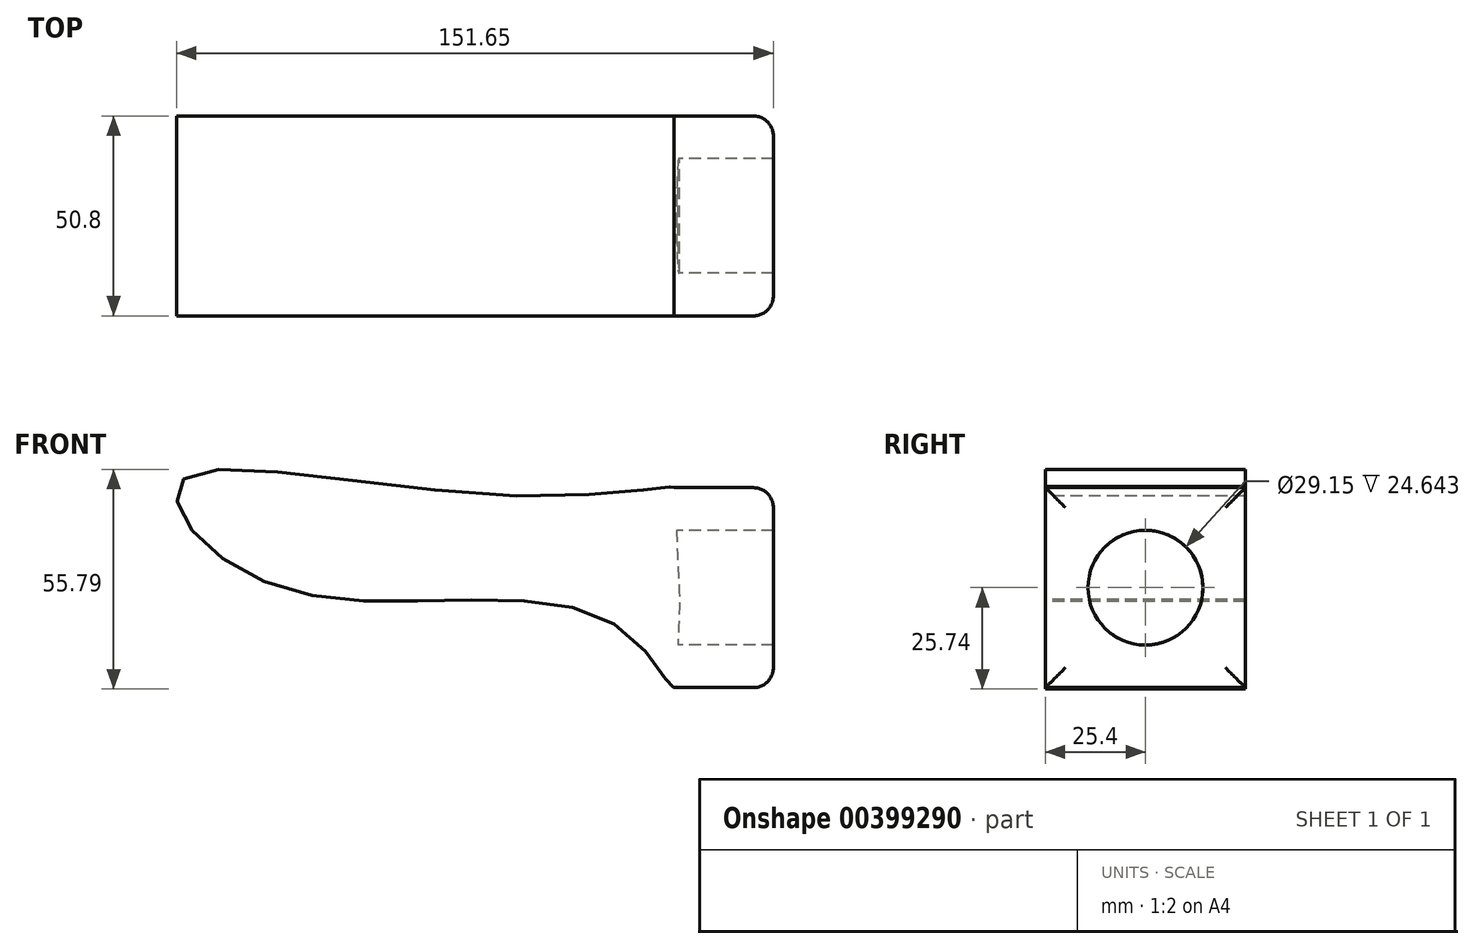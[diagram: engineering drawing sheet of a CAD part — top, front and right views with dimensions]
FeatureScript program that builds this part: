
annotation { "Feature Type Name" : "Feature", "Feature Type Description" : "" }
export const myFeature = defineFeature(function(context is Context, id is Id, definition is map)
    precondition{}
    {
        {
            var Q0;
            Q0=qCreatedBy(makeId("Right.planeOp"),FACE);
            var sketch = newSketch(context, id + "F0", { "sketchPlane" : qUnion([Q0])});
            skLineSegment(sketch, "E0.bottom", {"start": v(-25.4, 25.4) * mm, "end": v(25.4, 25.4) * mm});
            skLineSegment(sketch, "E0.top", {"start": v(-25.4, -25.4) * mm, "end": v(25.4, -25.4) * mm});
            skLineSegment(sketch, "E0.left", {"start": v(-25.4, 25.4) * mm, "end": v(-25.4, -25.4) * mm});
            skLineSegment(sketch, "E0.right", {"start": v(25.4, 25.4) * mm, "end": v(25.4, -25.4) * mm});
            skPoint(sketch, "E0.middle", {"position": v(0, 0) * mm});
            skSolve(sketch);
        }
        {
            var Q0;
            Q0=qCreatedBy(makeId("Front.planeOp"),FACE);
            var sketch = newSketch(context, id + "F1", { "sketchPlane" : qUnion([Q0])});
            skFitSpline(sketch, "E1", {"points": [v(0, 25.67) * mm, v(-0.64, 25.69) * mm, v(-0.66, 25.68) * mm, v(-43.43, 23.46) * mm, v(-123.44, 28.25) * mm, v(-124.91, 18.66) * mm, v(-99.84, 0) * mm, v(-51.9, -3.09) * mm, v(-13.2, -10.46) * mm, v(-0.63, -25.35) * mm, v(0, -25.58) * mm, v(1.53, -4.2) * mm, v(1.51, -2.72) * mm, v(0.19, 25.37) * mm, v(0, 25.67) * mm]});
            skSolve(sketch);
        }
        {
            var Q0;
            Q0=makeQuery(id+"F1.imprint","IMPRINT",FACE,{"disambiguationData":[TD([[makeQuery(id+"F1.imprint","IMPRINT",EDGE,{"derivedFrom":sQuery(id+"F1.wireOp",EDGE,"E1")}),1.0]])]});
            extrude(context, id + "F2", {"entities" : qUnion([Q0]), "depth" : 25.4 * mm, "hasSecondDirection" : true, "secondDirectionOppositeDirection" : true, "secondDirectionDepth" : 25.4 * mm});
        }
        {
            var Q0;
            Q0=makeQuery(id+"F0.imprint","IMPRINT",FACE,{"disambiguationData":[TD([[makeQuery(id+"F0.imprint","IMPRINT",EDGE,{"derivedFrom":sQuery(id+"F0.wireOp",EDGE,"E0.bottom")}),-1.0]])]});
            var sketch = newSketch(context, id + "F3", { "sketchPlane" : qUnion([Q0])});
            skCircle(sketch, "E2", {"center": v(0, 0) * mm, "radius": 14.57 * mm});
            skSolve(sketch);
        }
        {
            var Q0;
            Q0=makeQuery(id+"F3.imprint","IMPRINT",FACE,{"disambiguationData":[TD([[makeQuery(id+"F3.imprint","IMPRINT",EDGE,{"derivedFrom":sQuery(id+"F3.wireOp",EDGE,"E2")}),-1.0]])]});
            var Q1;
            Q1=sQuery(id+"F3.wireOp",EDGE,"E2");
            extrude(context, id + "F4", {"entities" : qUnion([Q0]), "operationType" : NewBodyOperationType.ADD, "surfaceEntities" : qUnion([Q1]), "depth" : 25.4 * mm});
        }
        {
            var Q0;
            Q0=makeQuery(id+"F4.opExtrude","CAP_EDGE",EDGE,{"disambiguationData":[OSD([sQuery(id+"F0.wireOp",EDGE,"E0.bottom")])],"isStart":false});
            var Q1;
            Q1=makeQuery(id+"F4.opExtrude","CAP_EDGE",EDGE,{"disambiguationData":[OSD([sQuery(id+"F0.wireOp",EDGE,"E0.right")])],"isStart":false});
            var Q2;
            Q2=makeQuery(id+"F4.opExtrude","CAP_EDGE",EDGE,{"disambiguationData":[OSD([sQuery(id+"F0.wireOp",EDGE,"E0.top")])],"isStart":false});
            var Q3;
            Q3=makeQuery(id+"F4.opExtrude","CAP_EDGE",EDGE,{"disambiguationData":[OSD([sQuery(id+"F0.wireOp",EDGE,"E0.left")])],"isStart":false});
            var Q4;
            Q4=makeQuery(id+"F4.opExtrude","CAP_EDGE",EDGE,{"disambiguationData":[OSD([sQuery(id+"F0.wireOp",EDGE,"E0.right")])],"isStart":true});
            var Q5;
            Q5=makeQuery(id+"F4.opExtrude","CAP_EDGE",EDGE,{"disambiguationData":[OSD([sQuery(id+"F0.wireOp",EDGE,"E0.left")])],"isStart":true});
            fillet(context, id + "F5", {"entities" : qUnion([Q0, Q1, Q2, Q3, Q4, Q5]), "radius" : 5.08 * mm, "tangentPropagation" : true, "allowEdgeOverflow" : false});
        }
    });
